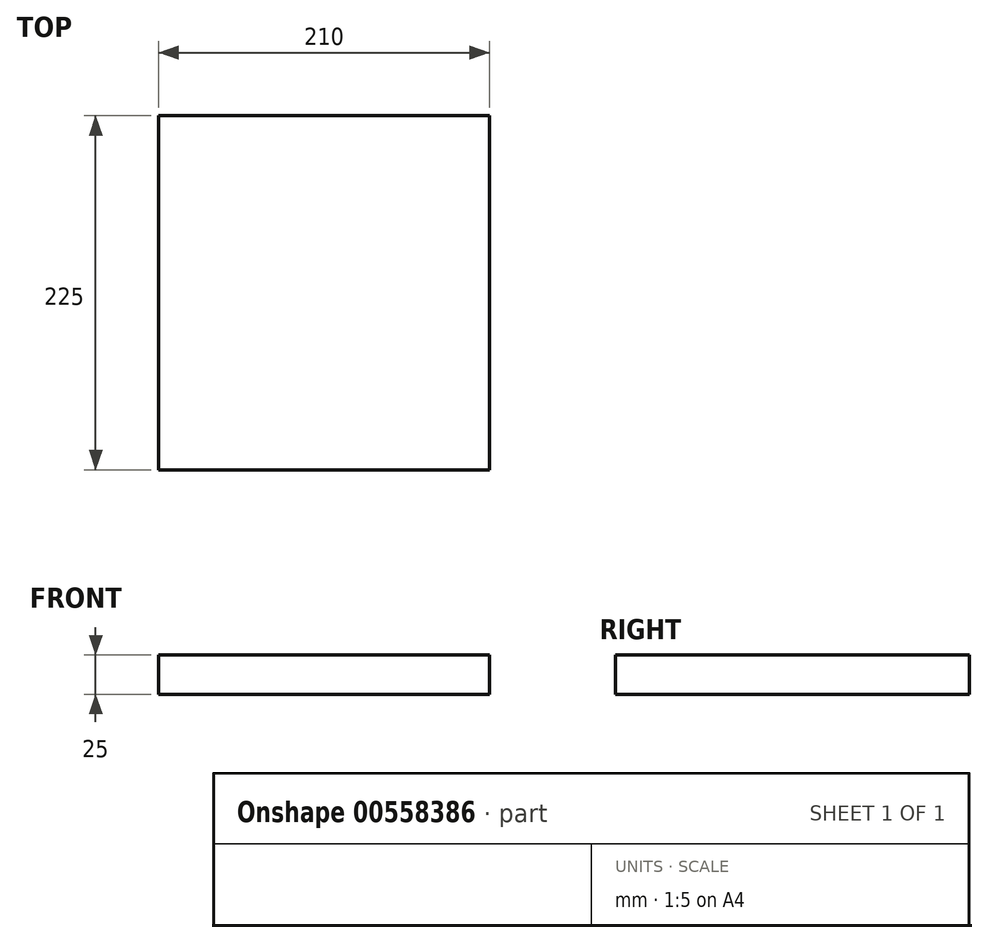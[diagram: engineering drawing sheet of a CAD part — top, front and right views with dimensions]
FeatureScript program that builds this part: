
annotation { "Feature Type Name" : "Feature", "Feature Type Description" : "" }
export const myFeature = defineFeature(function(context is Context, id is Id, definition is map)
    precondition{}
    {
        {
            var Q0;
            Q0=qCreatedBy(makeId("Top.planeOp"),FACE);
            var sketch = newSketch(context, id + "F0", { "sketchPlane" : qUnion([Q0])});
            skLineSegment(sketch, "E0.bottom", {"start": v(105, -112.5) * mm, "end": v(-105, -112.5) * mm});
            skLineSegment(sketch, "E0.top", {"start": v(105, 112.5) * mm, "end": v(-105, 112.5) * mm});
            skLineSegment(sketch, "E0.left", {"start": v(105, -112.5) * mm, "end": v(105, 112.5) * mm});
            skLineSegment(sketch, "E0.right", {"start": v(-105, -112.5) * mm, "end": v(-105, 112.5) * mm});
            skPoint(sketch, "E0.middle", {"position": v(0, 0) * mm});
            skSolve(sketch);
        }
        {
            var Q0;
            Q0=makeQuery(id+"F0.imprint","IMPRINT",FACE,{"disambiguationData":[TD([[makeQuery(id+"F0.imprint","IMPRINT",EDGE,{"derivedFrom":sQuery(id+"F0.wireOp",EDGE,"E0.bottom")}),-1.0]])]});
            extrude(context, id + "F1", {"entities" : qUnion([Q0]), "depth" : 25 * mm, "offsetDistance" : 25 * mm});
        }
    });
